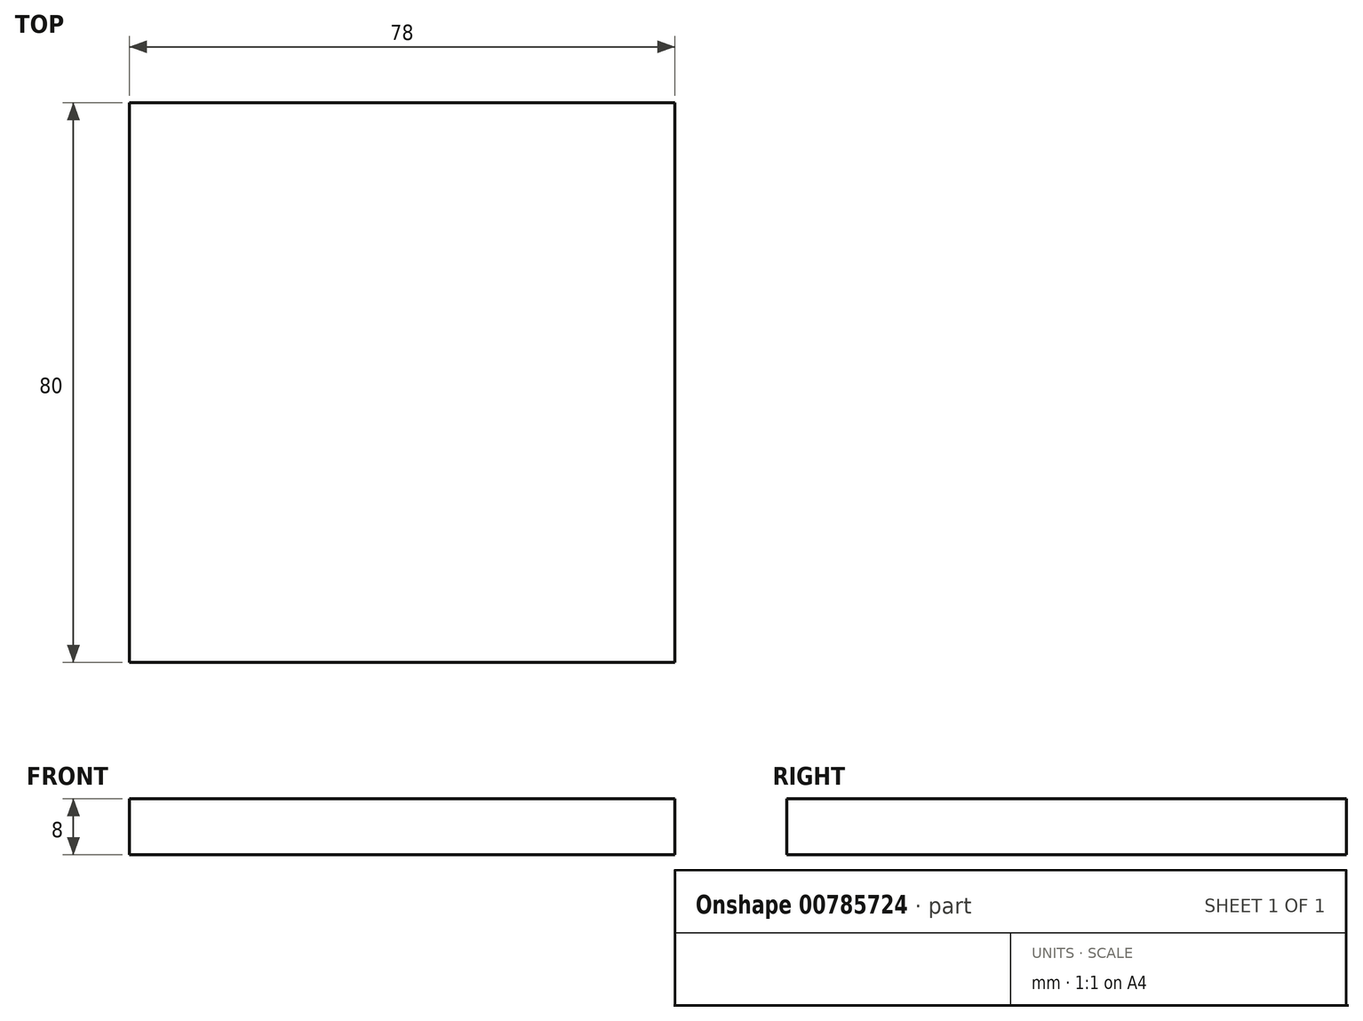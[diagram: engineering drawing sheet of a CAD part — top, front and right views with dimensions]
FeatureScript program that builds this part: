
annotation { "Feature Type Name" : "Feature", "Feature Type Description" : "" }
export const myFeature = defineFeature(function(context is Context, id is Id, definition is map)
    precondition{}
    {
        {
            var Q0;
            Q0=qCreatedBy(makeId("Top.planeOp"),FACE);
            var sketch = newSketch(context, id + "F0", { "sketchPlane" : qUnion([Q0])});
            skLineSegment(sketch, "E0.bottom", {"start": v(39, -40) * mm, "end": v(-39, -40) * mm});
            skLineSegment(sketch, "E0.top", {"start": v(39, 40) * mm, "end": v(-39, 40) * mm});
            skLineSegment(sketch, "E0.left", {"start": v(39, -40) * mm, "end": v(39, 40) * mm});
            skLineSegment(sketch, "E0.right", {"start": v(-39, -40) * mm, "end": v(-39, 40) * mm});
            skPoint(sketch, "E0.middle", {"position": v(0, 0) * mm});
            skSolve(sketch);
        }
        {
            var Q0;
            Q0 = qSketchRegion(id + "F0", true);
            extrude(context, id + "F1", {"entities" : qUnion([Q0]), "depth" : 8 * mm, "offsetDistance" : 25 * mm});
        }
    });
